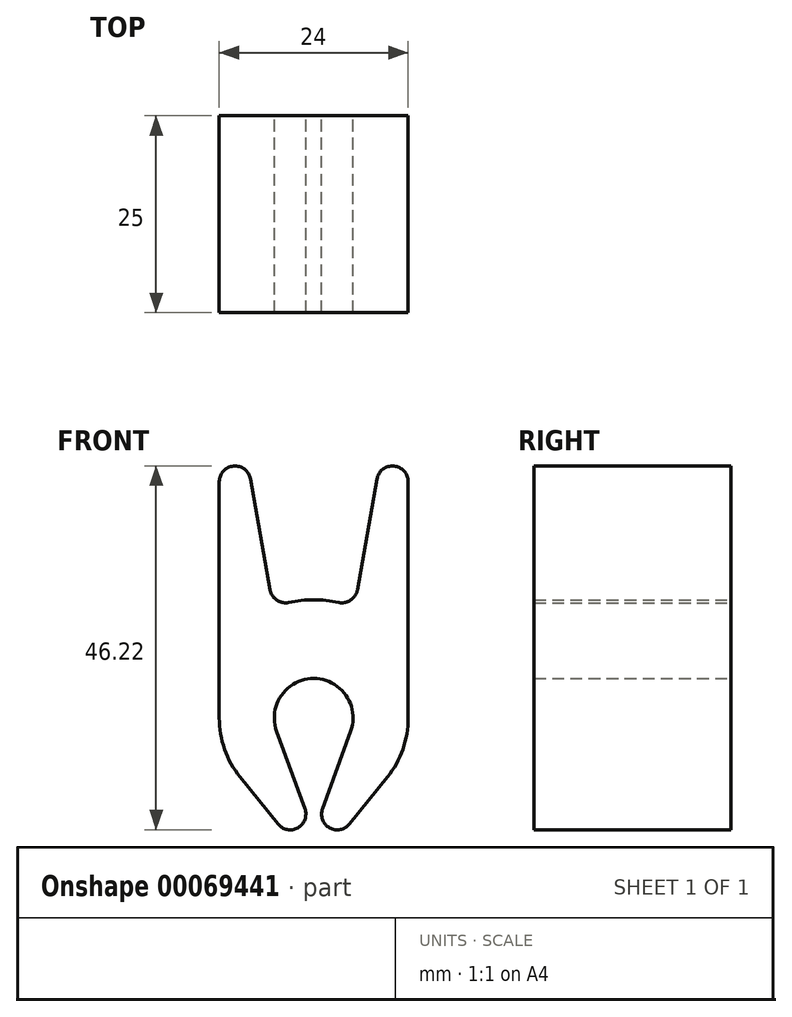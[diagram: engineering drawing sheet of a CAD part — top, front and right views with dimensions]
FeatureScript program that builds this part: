
annotation { "Feature Type Name" : "Feature", "Feature Type Description" : "" }
export const myFeature = defineFeature(function(context is Context, id is Id, definition is map)
    precondition{}
    {
        {
            var Q0;
            Q0=qCreatedBy(makeId("Front.planeOp"),FACE);
            var sketch = newSketch(context, id + "F0", { "sketchPlane" : qUnion([Q0])});
            skCircle(sketch, "E0", {"center": v(0, 0) * mm, "radius": 5 * mm});
            skLineSegment(sketch, "E1", {"start": v(4.7, -1.71) * mm, "end": v(1.12, -11.54) * mm});
            skArc(sketch, "E2", {"start": v(1.12, -11.54) * mm, "mid": v(2.02, -13.97) * mm, "end": v(4.56, -13.48) * mm});
            skLineSegment(sketch, "E3", {"start": v(4.56, -13.48) * mm, "end": v(9.35, -7.52) * mm});
            skLineSegment(sketch, "E4", {"start": v(1, -6.56) * mm, "end": v(1, -10.08) * mm, "construction": true});
            skArc(sketch, "E5", {"start": v(9.35, -7.52) * mm, "mid": v(11.32, -3.99) * mm, "end": v(12, 0) * mm});
            skLineSegment(sketch, "E6", {"start": v(12, 0) * mm, "end": v(12, 30) * mm});
            skArc(sketch, "E7", {"start": v(0, 15) * mm, "mid": v(1.59, 14.92) * mm, "end": v(3.16, 14.66) * mm});
            skArc(sketch, "E8", {"start": v(3.16, 14.66) * mm, "mid": v(4.7, 14.96) * mm, "end": v(5.55, 16.27) * mm});
            skLineSegment(sketch, "E9", {"start": v(5.55, 16.27) * mm, "end": v(8.03, 30.35) * mm});
            skArc(sketch, "E10", {"start": v(12, 30) * mm, "mid": v(10.17, 32) * mm, "end": v(8.03, 30.35) * mm});
            skLineSegment(sketch, "E11", {"start": v(0, 15) * mm, "end": v(0, 5) * mm});
            skSolve(sketch);
        }
        {
            var Q0;
            {var subQ0=sQuery(id+"F0.wireOp",EDGE,"E1");Q0=makeQuery(id+"F0.imprint","IMPRINT",FACE,{"disambiguationData":[TD([[makeQuery(id+"F0.imprint","IMPRINT",EDGE,{"derivedFrom":subQ0}),1.0]])]});}
            extrude(context, id + "F1", {"entities" : qUnion([Q0]), "depth" : 25 * mm});
        }
        {
            var Q0;
            Q0=makeQuery(id+"F1.opExtrude","SWEPT_BODY",BODY,{"disambiguationData":[OSD([sQuery(id+"F0.wireOp",EDGE,"E0"),sQuery(id+"F0.wireOp",EDGE,"E1"),sQuery(id+"F0.wireOp",EDGE,"E2"),sQuery(id+"F0.wireOp",EDGE,"E3"),sQuery(id+"F0.wireOp",EDGE,"E5"),sQuery(id+"F0.wireOp",EDGE,"E6"),sQuery(id+"F0.wireOp",EDGE,"E7"),sQuery(id+"F0.wireOp",EDGE,"E8"),sQuery(id+"F0.wireOp",EDGE,"E9"),sQuery(id+"F0.wireOp",EDGE,"E10"),sQuery(id+"F0.wireOp",EDGE,"E11")])]});
            var Q1;
            Q1=makeQuery(id+"F1.opExtrude","SWEPT_FACE",FACE,{"disambiguationData":[OSD([sQuery(id+"F0.wireOp",EDGE,"E11")])]});
            mirror(context, id + "F2", {"operationType" : NewBodyOperationType.ADD, "entities" : qUnion([Q0]), "mirrorPlane" : qUnion([Q1])});
        }
    });
